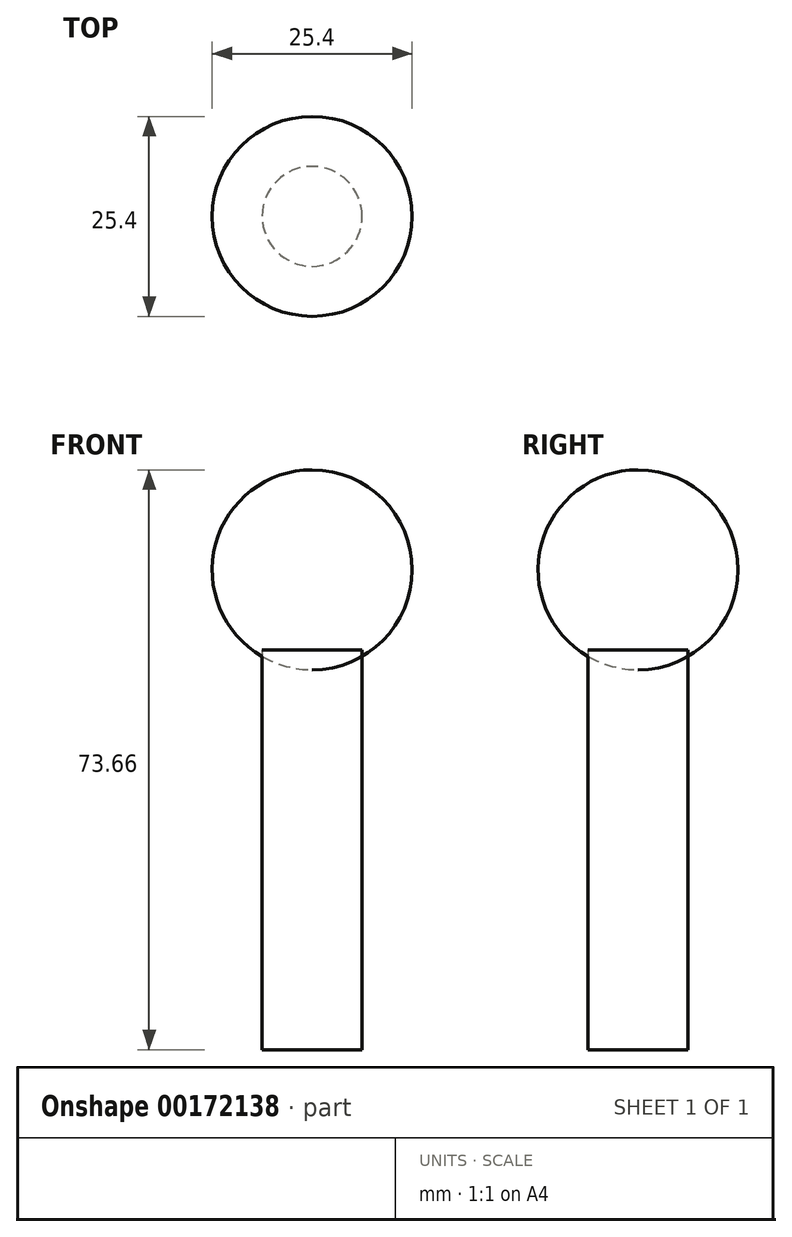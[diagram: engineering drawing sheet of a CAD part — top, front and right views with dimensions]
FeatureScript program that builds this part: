
annotation { "Feature Type Name" : "Feature", "Feature Type Description" : "" }
export const myFeature = defineFeature(function(context is Context, id is Id, definition is map)
    precondition{}
    {
        {
            var Q0;
            Q0=qCreatedBy(makeId("Top.planeOp"),FACE);
            var sketch = newSketch(context, id + "F0", { "sketchPlane" : qUnion([Q0])});
            skCircle(sketch, "E0", {"center": v(0, 0) * mm, "radius": 6.35 * mm});
            skSolve(sketch);
        }
        {
            var Q0;
            Q0=makeQuery(id+"F0.imprint","IMPRINT",FACE,{"disambiguationData":[TD([[makeQuery(id+"F0.imprint","IMPRINT",EDGE,{"derivedFrom":sQuery(id+"F0.wireOp",EDGE,"E0")}),1.0]])]});
            extrude(context, id + "F1", {"entities" : qUnion([Q0]), "endBound" : BoundingType.SYMMETRIC, "depth" : 50.8 * mm});
        }
        {
            var Q0;
            Q0=qCreatedBy(makeId("Front.planeOp"),FACE);
            var sketch = newSketch(context, id + "F2", { "sketchPlane" : qUnion([Q0])});
            skLineSegment(sketch, "E1", {"start": v(0, 22.86) * mm, "end": v(0, 48.26) * mm});
            skArc(sketch, "E2", {"start": v(0, 22.86) * mm, "mid": v(12.7, 35.56) * mm, "end": v(0, 48.26) * mm});
            skArc(sketch, "E3.MirrorCS", {"start": v(0, -22.86) * mm, "mid": v(12.7, -35.56) * mm, "end": v(0, -48.26) * mm});
            skLineSegment(sketch, "E4.MirrorCS", {"start": v(0, -22.86) * mm, "end": v(0, -48.26) * mm});
            skSolve(sketch);
        }
        {
            var Q0;
            Q0=makeQuery(id+"F2.imprint","IMPRINT",FACE,{"disambiguationData":[TD([[makeQuery(id+"F2.imprint","IMPRINT",EDGE,{"derivedFrom":sQuery(id+"F2.wireOp",EDGE,"E1")}),-1.0]])]});
            var Q1;
            Q1=makeQuery(id+"F2.imprint","IMPRINT",FACE,{"disambiguationData":[TD([[makeQuery(id+"F2.imprint","IMPRINT",EDGE,{"derivedFrom":sQuery(id+"F2.wireOp",EDGE,"E3.MirrorCS")}),-1.0]])]});
            var Q2;
            Q2=sQuery(id+"F2.wireOp",EDGE,"E1");
            revolve(context, id + "F3", {"entities" : qUnion([Q0, Q1]), "axis" : qUnion([Q2]), "revolveType" : RevolveType.FULL});
        }
    });
